# Revit family: CM
name_source: partatom
category: Specialty Equipment
revit_build: Autodesk Revit Architecture 2015 (Build: 20141119_1515(x64)
units: mm (PartAtom-declared; Revit-internal decimal feet)

## types (9) — shared parameters
Curb = 0' - 3"
Description = Mechanical Leveler
LipExtension = 0' - 0"
LipLength = 1' - 6"
Manufacturer = Kelley Entrematic
Model = CM
URL = http://kelleyentrematic.com

## per-type parameters (varying)
| type | PitDepth | PitDepthR | PitLength | PitWidth |
| 6x6 | 1' - 8" | 1' - 7 1/2" | 5' - 3" | 6' - 1" |
| 6x8 | 1' - 8" | 1' - 7 1/2" | 7' - 3" | 6' - 1" |
| 6.5x6 | 1' - 8" | 1' - 7 1/2" | 5' - 3" | 6' - 7" |
| 6.5x8 | 1' - 8" | 1' - 7 1/2" | 7' - 3" | 6' - 7" |
| 7x6 | 1' - 8" | 1' - 7 1/2" | 5' - 3" | 7' - 1" |
| 7x8 | 1' - 8" | 1' - 7 1/2" | 7' - 3" | 7' - 1" |
| 6x10 | 2' - 0" | 1' - 11 1/2" | 9' - 3" | 6' - 1" |
| 6.5x10 | 2' - 0" | 1' - 11 1/2" | 9' - 3" | 6' - 7" |
| 7x10 | 2' - 0" | 1' - 11 1/2" | 9' - 3" | 7' - 1" |

## geometry (parser evidence)
native form markers: Blend x4, Sweep x2
no freeform markers — native parametric forms only
